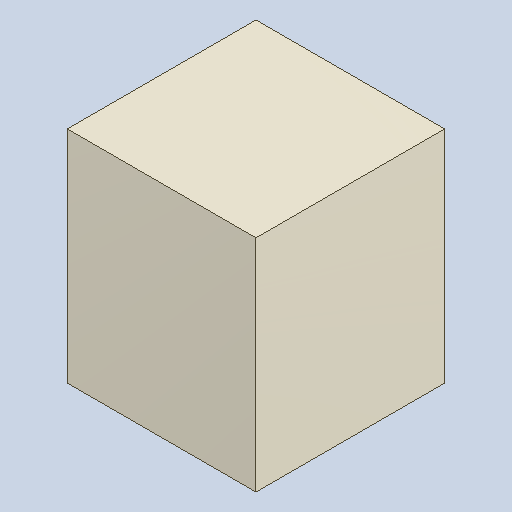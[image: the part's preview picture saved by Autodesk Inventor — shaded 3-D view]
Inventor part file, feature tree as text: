
AUTODESK INVENTOR PART (.ipt)
format: ipt  version: 2023.4 (Build 274418000, 418)  size: 82,944 bytes
history: native  units: mm
features: extrude x1
ambient origin geometry x8: Origin, YZ Plane, XZ Plane, XY Plane, X Axis, Y Axis, Z Axis, Center Point
bodies: Solid1 (feature_tree)
feature tree (1):
  extrude  "Extruded_30"  [1 undecoded]
note: 1 required parameter value undecoded (feature->parameter linkage not recoverable at this tier; creation-order binding heuristic only, values carry confidence <= 0.55)
